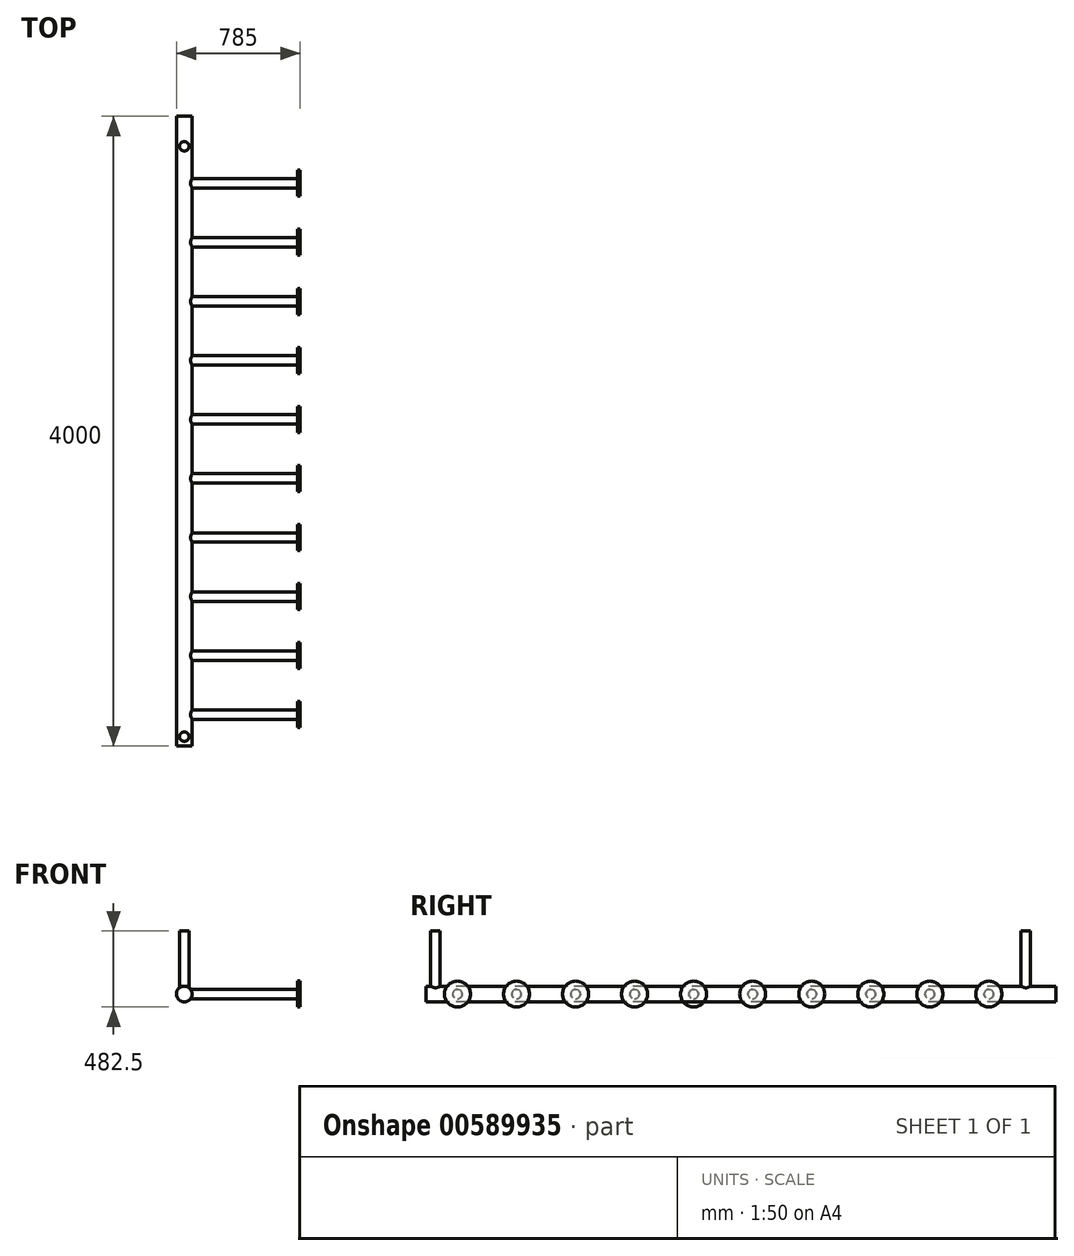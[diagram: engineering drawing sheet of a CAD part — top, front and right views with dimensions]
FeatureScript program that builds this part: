
annotation { "Feature Type Name" : "Feature", "Feature Type Description" : "" }
export const myFeature = defineFeature(function(context is Context, id is Id, definition is map)
    precondition{}
    {
        {
            var Q0;
            Q0=qCreatedBy(makeId("Front.planeOp"),FACE);
            var sketch = newSketch(context, id + "F0", { "sketchPlane" : qUnion([Q0])});
            skCircle(sketch, "E0", {"center": v(0, 0) * mm, "radius": 50 * mm});
            skSolve(sketch);
        }
        {
            var Q0;
            Q0=makeQuery(id+"F0.imprint","IMPRINT",FACE,{"disambiguationData":[TD([[makeQuery(id+"F0.imprint","IMPRINT",EDGE,{"derivedFrom":sQuery(id+"F0.wireOp",EDGE,"E0")}),1.0]])]});
            extrude(context, id + "F1", {"entities" : qUnion([Q0]), "oppositeDirection" : true, "depth" : 4000 * mm, "offsetDistance" : 25 * mm});
        }
        {
            var Q0;
            Q0=qCreatedBy(makeId("Top.planeOp"),FACE);
            var sketch = newSketch(context, id + "F2", { "sketchPlane" : qUnion([Q0])});
            skCircle(sketch, "E1", {"center": v(0, 60) * mm, "radius": 30 * mm});
            skCircle(sketch, "E2", {"center": v(0, 3810) * mm, "radius": 30 * mm});
            skSolve(sketch);
        }
        {
            var Q0;
            Q0 = qSketchRegion(id + "F2", true);
            extrude(context, id + "F3", {"entities" : qUnion([Q0]), "operationType" : NewBodyOperationType.ADD, "depth" : 400 * mm, "offsetDistance" : 25 * mm});
        }
        {
            var Q0;
            Q0=qCreatedBy(makeId("Right.planeOp"),FACE);
            var sketch = newSketch(context, id + "F4", { "sketchPlane" : qUnion([Q0])});
            skCircle(sketch, "E3", {"center": v(200, 0) * mm, "radius": 30 * mm});
            skCircle(sketch, "E4.1.0.0", {"center": v(575, 0) * mm, "radius": 30 * mm});
            skCircle(sketch, "E4.2.0.0", {"center": v(950, 0) * mm, "radius": 30 * mm});
            skCircle(sketch, "E4.3.0.0", {"center": v(1325, 0) * mm, "radius": 30 * mm});
            skCircle(sketch, "E4.4.0.0", {"center": v(1700, 0) * mm, "radius": 30 * mm});
            skCircle(sketch, "E4.5.0.0", {"center": v(2075, 0) * mm, "radius": 30 * mm});
            skCircle(sketch, "E4.6.0.0", {"center": v(2450, 0) * mm, "radius": 30 * mm});
            skCircle(sketch, "E4.7.0.0", {"center": v(2825, 0) * mm, "radius": 30 * mm});
            skCircle(sketch, "E4.8.0.0", {"center": v(3200, 0) * mm, "radius": 30 * mm});
            skCircle(sketch, "E4.9.0.0", {"center": v(3575, 0) * mm, "radius": 30 * mm});
            skLineSegment(sketch, "E4.direction1", {"start": v(200, 0) * mm, "end": v(575, 0) * mm, "construction": true});
            skSolve(sketch);
        }
        {
            var Q0;
            Q0 = qSketchRegion(id + "F4", true);
            extrude(context, id + "F5", {"entities" : qUnion([Q0]), "operationType" : NewBodyOperationType.ADD, "depth" : 720 * mm, "offsetDistance" : 25 * mm});
        }
        {
            var Q0;
            Q0=makeQuery(id+"F5.opExtrude","CAP_FACE",FACE,{"disambiguationData":[OSD([sQuery(id+"F4.wireOp",EDGE,"E3")])],"isStart":false});
            var sketch = newSketch(context, id + "F6", { "sketchPlane" : qUnion([Q0])});
            skCircle(sketch, "E5", {"center": v(200, 0) * mm, "radius": 82.5 * mm});
            skCircle(sketch, "E6.1.0.0", {"center": v(575, 0) * mm, "radius": 82.5 * mm});
            skCircle(sketch, "E6.2.0.0", {"center": v(950, 0) * mm, "radius": 82.5 * mm});
            skCircle(sketch, "E6.3.0.0", {"center": v(1325, 0) * mm, "radius": 82.5 * mm});
            skCircle(sketch, "E6.4.0.0", {"center": v(1700, 0) * mm, "radius": 82.5 * mm});
            skCircle(sketch, "E6.5.0.0", {"center": v(2075, 0) * mm, "radius": 82.5 * mm});
            skCircle(sketch, "E6.6.0.0", {"center": v(2450, 0) * mm, "radius": 82.5 * mm});
            skCircle(sketch, "E6.7.0.0", {"center": v(2825, 0) * mm, "radius": 82.5 * mm});
            skCircle(sketch, "E6.8.0.0", {"center": v(3200, 0) * mm, "radius": 82.5 * mm});
            skCircle(sketch, "E6.9.0.0", {"center": v(3575, 0) * mm, "radius": 82.5 * mm});
            skLineSegment(sketch, "E6.direction1", {"start": v(200, 0) * mm, "end": v(575, 0) * mm, "construction": true});
            skSolve(sketch);
        }
        {
            var Q0;
            Q0 = qSketchRegion(id + "F6", true);
            extrude(context, id + "F7", {"entities" : qUnion([Q0]), "operationType" : NewBodyOperationType.ADD, "depth" : 15 * mm, "offsetDistance" : 25 * mm});
        }
    });
